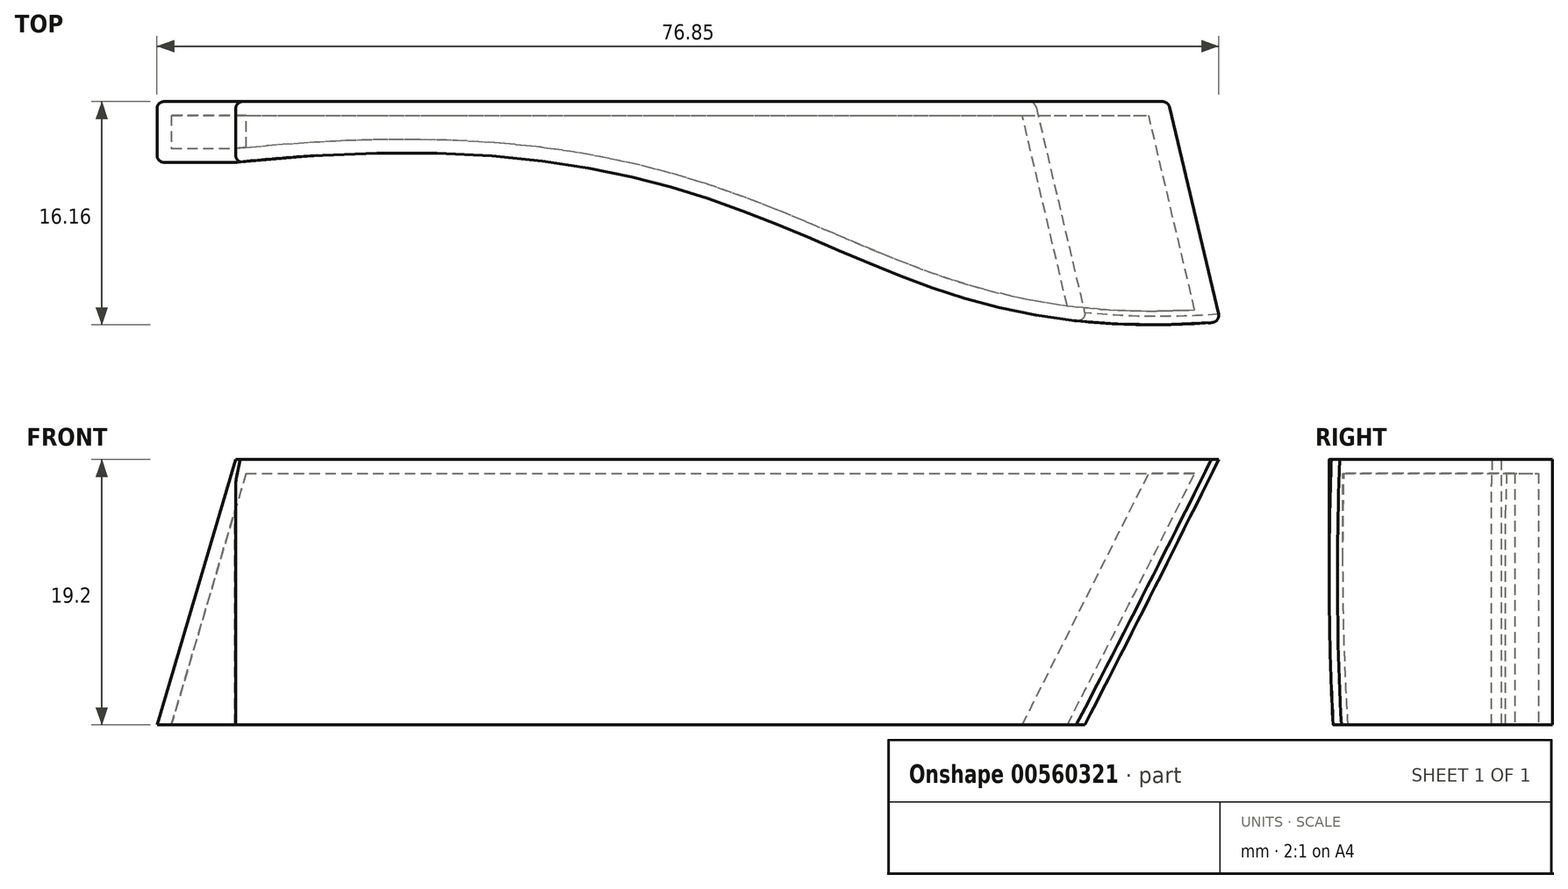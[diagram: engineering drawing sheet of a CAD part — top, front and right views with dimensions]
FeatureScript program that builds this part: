
annotation { "Feature Type Name" : "Feature", "Feature Type Description" : "" }
export const myFeature = defineFeature(function(context is Context, id is Id, definition is map)
    precondition{}
    {
        {
            var Q0;
            Q0=qCreatedBy(makeId("Top.planeOp"),FACE);
            var sketch = newSketch(context, id + "F0", { "sketchPlane" : qUnion([Q0])});
            skLineSegment(sketch, "E0", {"start": v(-41.96, 2.87) * mm, "end": v(-41.96, 7.27) * mm});
            skLineSegment(sketch, "E1", {"start": v(-41.96, 7.27) * mm, "end": v(25.54, 7.27) * mm});
            skLineSegment(sketch, "E2", {"start": v(25.54, 7.27) * mm, "end": v(29.3, -8.7) * mm});
            skFitSpline(sketch, "E3", {"points": [v(-41.96, 2.87) * mm, v(29.3, -8.7) * mm], "startDerivative": vector(125.88, 13.2) * mm, "endDerivative": vector(87.93, 6.81) * mm});
            skSolve(sketch);
        }
        {
            var Q0;
            Q0 = qSketchRegion(id + "F0", true);
            extrude(context, id + "F1", {"entities" : qUnion([Q0]), "oppositeDirection" : true, "depth" : 19.2 * mm, "offsetDistance" : 25 * mm});
        }
        {
            var Q0;
            Q0=makeQuery(id+"F1.opExtrude","SWEPT_FACE",FACE,{"disambiguationData":[OSD([sQuery(id+"F0.wireOp",EDGE,"E0")])]});
            var sketch = newSketch(context, id + "F2", { "sketchPlane" : qUnion([Q0])});
            skLineSegment(sketch, "E4.bottom", {"start": v(-2.87, -19.2) * mm, "end": v(-7.27, -19.2) * mm});
            skLineSegment(sketch, "E4.top", {"start": v(-2.87, 0) * mm, "end": v(-7.27, 0) * mm});
            skLineSegment(sketch, "E4.left", {"start": v(-2.87, -19.2) * mm, "end": v(-2.87, 0) * mm});
            skLineSegment(sketch, "E4.right", {"start": v(-7.27, -19.2) * mm, "end": v(-7.27, 0) * mm});
            skSolve(sketch);
        }
        {
            var Q0;
            Q0 = qSketchRegion(id + "F2", true);
            extrude(context, id + "F3", {"entities" : qUnion([Q0]), "operationType" : NewBodyOperationType.ADD, "depth" : 5.7 * mm, "offsetDistance" : 25 * mm});
        }
        {
            var Q0;
            Q0=makeQuery(id+"F3.opExtrude","CAP_EDGE",EDGE,{"disambiguationData":[OSD([sQuery(id+"F2.wireOp",EDGE,"E4.top")])],"isStart":false});
            chamfer(context, id + "F4", {"entities" : qUnion([Q0]), "chamferType" : ChamferType.TWO_OFFSETS, "width1" : 19.2 * mm, "oppositeDirection" : false, "width2" : 5.7 * mm, "tangentPropagation" : true});
        }
        {
            var Q0;
            Q0=makeQuery(id+"F1.opExtrude","CAP_EDGE",EDGE,{"disambiguationData":[OSD([sQuery(id+"F0.wireOp",EDGE,"E2")])],"isStart":false});
            chamfer(context, id + "F5", {"entities" : qUnion([Q0]), "chamferType" : ChamferType.TWO_OFFSETS, "width1" : 9.4 * mm, "oppositeDirection" : false, "width2" : 19.2 * mm, "tangentPropagation" : true});
        }
        {
            var Q0;
            Q0=makeQuery(id+"F3.boolean.opBoolean","MERGE",FACE,{"derivedFrom":[makeQuery(id+"F1.opExtrude","CAP_FACE",FACE,{"disambiguationData":[OSD([sQuery(id+"F0.wireOp",EDGE,"E0"),sQuery(id+"F0.wireOp",EDGE,"E1"),sQuery(id+"F0.wireOp",EDGE,"E2"),sQuery(id+"F0.wireOp",EDGE,"E3")])],"isStart":false}),makeQuery(id+"F3.opExtrude","SWEPT_FACE",FACE,{"disambiguationData":[OSD([sQuery(id+"F2.wireOp",EDGE,"E4.bottom")])]})]});
            shell(context, id + "F6", {"entities" : qUnion([Q0]), "thickness" : 1 * mm});
        }
        {
            var Q0;
            Q0=makeQuery(id+"F5.opChamfer","BLEND_EDGE",EDGE,{"blendedFrom":[makeQuery(id+"F1.opExtrude","CAP_EDGE",EDGE,{"disambiguationData":[OSD([sQuery(id+"F0.wireOp",EDGE,"E2")])],"isStart":false}),makeQuery(id+"F3.boolean.opBoolean","MERGE",FACE,{"derivedFrom":[makeQuery(id+"F1.opExtrude","SWEPT_FACE",FACE,{"disambiguationData":[OSD([sQuery(id+"F0.wireOp",EDGE,"E1")])]}),makeQuery(id+"F3.opExtrude","SWEPT_FACE",FACE,{"disambiguationData":[OSD([sQuery(id+"F2.wireOp",EDGE,"E4.right")])]})]})],"blendedInto":[makeQuery(id+"F3.boolean.opBoolean","MERGE",FACE,{"derivedFrom":[makeQuery(id+"F1.opExtrude","SWEPT_FACE",FACE,{"disambiguationData":[OSD([sQuery(id+"F0.wireOp",EDGE,"E1")])]}),makeQuery(id+"F3.opExtrude","SWEPT_FACE",FACE,{"disambiguationData":[OSD([sQuery(id+"F2.wireOp",EDGE,"E4.right")])]})]})]});
            var Q1;
            Q1=makeQuery(id+"F4.opChamfer","BLEND_EDGE",EDGE,{"blendedFrom":[makeQuery(id+"F3.opExtrude","CAP_EDGE",EDGE,{"disambiguationData":[OSD([sQuery(id+"F2.wireOp",EDGE,"E4.top")])],"isStart":false}),makeQuery(id+"F3.boolean.opBoolean","MERGE",FACE,{"derivedFrom":[makeQuery(id+"F1.opExtrude","SWEPT_FACE",FACE,{"disambiguationData":[OSD([sQuery(id+"F0.wireOp",EDGE,"E1")])]}),makeQuery(id+"F3.opExtrude","SWEPT_FACE",FACE,{"disambiguationData":[OSD([sQuery(id+"F2.wireOp",EDGE,"E4.right")])]})]})],"blendedInto":[makeQuery(id+"F3.boolean.opBoolean","MERGE",FACE,{"derivedFrom":[makeQuery(id+"F1.opExtrude","SWEPT_FACE",FACE,{"disambiguationData":[OSD([sQuery(id+"F0.wireOp",EDGE,"E1")])]}),makeQuery(id+"F3.opExtrude","SWEPT_FACE",FACE,{"disambiguationData":[OSD([sQuery(id+"F2.wireOp",EDGE,"E4.right")])]})]})]});
            var Q2;
            Q2=makeQuery(id+"F5.opChamfer","BLEND_EDGE",EDGE,{"blendedFrom":[makeQuery(id+"F1.opExtrude","CAP_EDGE",EDGE,{"disambiguationData":[OSD([sQuery(id+"F0.wireOp",EDGE,"E2")])],"isStart":false}),makeQuery(id+"F1.opExtrude","SWEPT_FACE",FACE,{"disambiguationData":[OSD([sQuery(id+"F0.wireOp",EDGE,"E3")])]})],"blendedInto":[makeQuery(id+"F1.opExtrude","SWEPT_FACE",FACE,{"disambiguationData":[OSD([sQuery(id+"F0.wireOp",EDGE,"E3")])]})]});
            var Q3;
            Q3=makeQuery(id+"F4.opChamfer","BLEND_EDGE",EDGE,{"blendedFrom":[makeQuery(id+"F3.opExtrude","CAP_EDGE",EDGE,{"disambiguationData":[OSD([sQuery(id+"F2.wireOp",EDGE,"E4.top")])],"isStart":false}),makeQuery(id+"F3.opExtrude","SWEPT_FACE",FACE,{"disambiguationData":[OSD([sQuery(id+"F2.wireOp",EDGE,"E4.left")])]})],"blendedInto":[makeQuery(id+"F3.opExtrude","SWEPT_FACE",FACE,{"disambiguationData":[OSD([sQuery(id+"F2.wireOp",EDGE,"E4.left")])]})]});
            fillet(context, id + "F7", {"entities" : qUnion([Q0, Q1, Q2, Q3]), "radius" : 0.5 * mm, "tangentPropagation" : true, "allowEdgeOverflow" : false});
        }
    });
